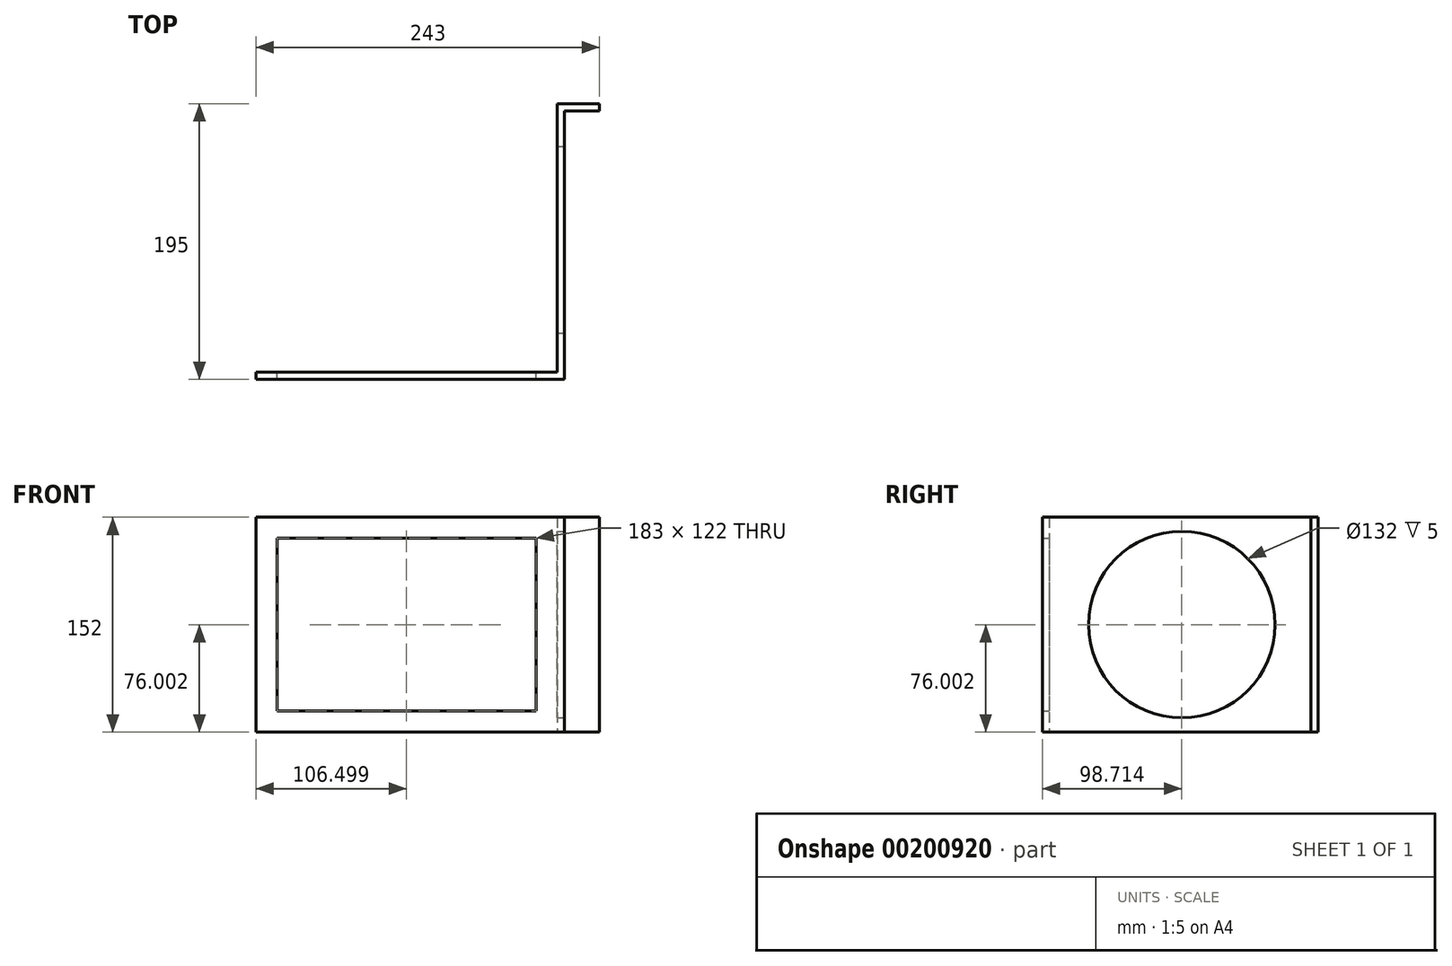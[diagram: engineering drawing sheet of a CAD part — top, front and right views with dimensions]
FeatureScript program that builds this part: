
annotation { "Feature Type Name" : "Feature", "Feature Type Description" : "" }
export const myFeature = defineFeature(function(context is Context, id is Id, definition is map)
    precondition{}
    {
        {
            var Q0;
            Q0=qCreatedBy(makeId("Front.planeOp"),FACE);
            var sketch = newSketch(context, id + "F0", { "sketchPlane" : qUnion([Q0])});
            skLineSegment(sketch, "E0.bottom", {"start": v(-91.93, 67.4) * mm, "end": v(91.07, 67.4) * mm});
            skLineSegment(sketch, "E0.top", {"start": v(-91.93, -54.6) * mm, "end": v(91.07, -54.6) * mm});
            skLineSegment(sketch, "E0.left", {"start": v(-91.93, 67.4) * mm, "end": v(-91.93, -54.6) * mm});
            skLineSegment(sketch, "E0.right", {"start": v(91.07, 67.4) * mm, "end": v(91.07, -54.6) * mm});
            skLineSegment(sketch, "E1.bottom", {"start": v(-106.93, 82.4) * mm, "end": v(106.07, 82.4) * mm});
            skLineSegment(sketch, "E1.top", {"start": v(-106.93, -69.6) * mm, "end": v(106.07, -69.6) * mm});
            skLineSegment(sketch, "E1.left", {"start": v(-106.93, 82.4) * mm, "end": v(-106.93, -69.6) * mm});
            skLineSegment(sketch, "E1.right", {"start": v(106.07, 82.4) * mm, "end": v(106.07, -69.6) * mm});
            skSolve(sketch);
        }
        {
            var Q0;
            Q0 = qSketchRegion(id + "F0", true);
            extrude(context, id + "F1", {"entities" : qUnion([Q0]), "depth" : 5 * mm});
        }
        {
            var Q0;
            Q0=makeQuery(id+"F1.opExtrude","SWEPT_FACE",FACE,{"disambiguationData":[OSD([sQuery(id+"F0.wireOp",EDGE,"E1.right")])]});
            var sketch = newSketch(context, id + "F2", { "sketchPlane" : qUnion([Q0])});
            skLineSegment(sketch, "E2.bottom", {"start": v(-5, 82.4) * mm, "end": v(185, 82.4) * mm});
            skLineSegment(sketch, "E2.top", {"start": v(-5, -69.6) * mm, "end": v(185, -69.6) * mm});
            skLineSegment(sketch, "E2.left", {"start": v(-5, 82.4) * mm, "end": v(-5, -69.6) * mm});
            skLineSegment(sketch, "E2.right", {"start": v(185, 82.4) * mm, "end": v(185, -69.6) * mm});
            skSolve(sketch);
        }
        {
            var Q0;
            {var subQ2=sQuery(id+"F2.wireOp",EDGE,"E2.right");Q0=makeQuery(id+"F2.imprint","IMPRINT",FACE,{"disambiguationData":[TD([[makeQuery(id+"F2.imprint","IMPRINT",EDGE,{"derivedFrom":subQ2}),-1.0]])]});}
            var Q1;
            {var subQ2=sQuery(id+"F2.wireOp",EDGE,"E2.left");Q1=makeQuery(id+"F2.imprint","IMPRINT",FACE,{"disambiguationData":[TD([[makeQuery(id+"F2.imprint","IMPRINT",EDGE,{"derivedFrom":subQ2}),1.0]])]});}
            extrude(context, id + "F3", {"entities" : qUnion([Q0, Q1]), "operationType" : NewBodyOperationType.ADD, "depth" : 5 * mm});
        }
        {
            var Q0;
            Q0=makeQuery(id+"F3.opExtrude","CAP_FACE",FACE,{"disambiguationData":[OSD([sQuery(id+"F2.wireOp",EDGE,"E2.bottom"),sQuery(id+"F2.wireOp",EDGE,"E2.top"),sQuery(id+"F2.wireOp",EDGE,"E2.left"),sQuery(id+"F2.wireOp",EDGE,"E2.right")])],"isStart":false});
            var sketch = newSketch(context, id + "F4", { "sketchPlane" : qUnion([Q0])});
            skCircle(sketch, "E3", {"center": v(93.71, 6.4) * mm, "radius": 66 * mm});
            skPoint(sketch, "E3.centerSnap0", {"position": v(185, 6.4) * mm});
            skSolve(sketch);
        }
        {
            var Q0;
            Q0=makeQuery(id+"F4.imprint","IMPRINT",FACE,{"disambiguationData":[TD([[makeQuery(id+"F4.imprint","IMPRINT",EDGE,{"derivedFrom":sQuery(id+"F4.wireOp",EDGE,"E3")}),1.0]])]});
            extrude(context, id + "F5", {"entities" : qUnion([Q0]), "operationType" : NewBodyOperationType.REMOVE, "oppositeDirection" : true, "depth" : 25 * mm});
        }
        {
            var Q0;
            Q0=makeQuery(id+"F3.opExtrude","SWEPT_FACE",FACE,{"disambiguationData":[OSD([sQuery(id+"F2.wireOp",EDGE,"E2.right")])]});
            var sketch = newSketch(context, id + "F6", { "sketchPlane" : qUnion([Q0])});
            skLineSegment(sketch, "E4.bottom", {"start": v(-106.07, 82.4) * mm, "end": v(-136.07, 82.4) * mm});
            skLineSegment(sketch, "E4.top", {"start": v(-106.07, -69.6) * mm, "end": v(-136.07, -69.6) * mm});
            skLineSegment(sketch, "E4.left", {"start": v(-106.07, 82.4) * mm, "end": v(-106.07, -69.6) * mm});
            skLineSegment(sketch, "E4.right", {"start": v(-136.07, 82.4) * mm, "end": v(-136.07, -69.6) * mm});
            skSolve(sketch);
        }
        {
            var Q0;
            {var subQ2=sQuery(id+"F6.wireOp",EDGE,"E4.right");Q0=makeQuery(id+"F6.imprint","IMPRINT",FACE,{"disambiguationData":[TD([[makeQuery(id+"F6.imprint","IMPRINT",EDGE,{"derivedFrom":subQ2}),1.0]])]});}
            var Q1;
            {var subQ0=sQuery(id+"F6.wireOp",EDGE,"E4.left");Q1=makeQuery(id+"F6.imprint","IMPRINT",FACE,{"disambiguationData":[TD([[makeQuery(id+"F6.imprint","IMPRINT",EDGE,{"derivedFrom":subQ0}),-1.0]])]});}
            extrude(context, id + "F7", {"entities" : qUnion([Q0, Q1]), "operationType" : NewBodyOperationType.ADD, "depth" : 5 * mm});
        }
    });
